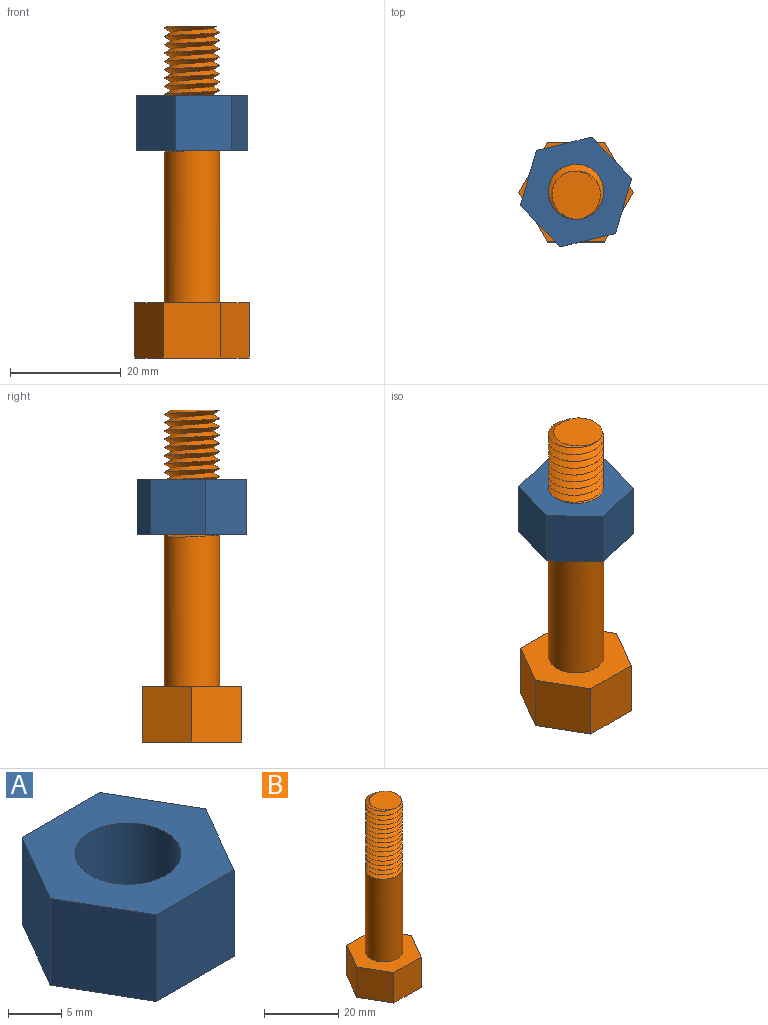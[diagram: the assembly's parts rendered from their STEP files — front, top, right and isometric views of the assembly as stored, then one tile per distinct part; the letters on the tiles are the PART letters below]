
ASSEMBLY  parts=2 mates=1
PART A: 9 faces, bbox 20.7x17.9x10 mm
  f0: plane 10x8.96mm, normal (0.87,-0.5,0), area 103.5mm2, adj f1,f5,f7,f8
  f1: plane 10x8.96mm, normal (0.87,0.5,0), area 103.5mm2, adj f0,f2,f7,f8
  f2: plane 10.35x10mm, normal (0,1,0), area 103.5mm2, adj f1,f3,f7,f8
  f3: plane 10x8.96mm, normal (-0.87,0.5,0), area 103.5mm2, adj f2,f4,f7,f8
  f4: plane 10x8.96mm, normal (-0.87,-0.5,0), area 103.5mm2, adj f3,f5,f7,f8
  f5: plane 10.35x10mm, normal (0,-1,0), area 103.5mm2, adj f0,f4,f7,f8
  f6: cylinder r=5mm len=10mm, axis (0,0,-1), area 314.2mm2, adj f7,f8
  f7: plane 20.7x17.93mm, normal (0,0,1), area 199.7mm2, adj f0,f1,f2,f3,f4,f5,f6
  f8: plane 20.7x17.93mm, normal (0,0,-1), area 199.7mm2, adj f0,f1,f2,f3,f4,f5,f6
PART B: 28 faces, bbox 21.8x19x61.9 mm
  f0: plane 10x8.96mm, normal (0.87,-0.5,0), area 103.5mm2, adj f1,f5,f6,f7
  f1: plane 10x8.96mm, normal (0.87,0.5,0), area 103.5mm2, adj f0,f2,f6,f7
  f2: plane 10.35x10mm, normal (0,1,0), area 103.5mm2, adj f1,f3,f6,f7
  f3: plane 10x8.96mm, normal (-0.87,0.5,0), area 103.5mm2, adj f2,f4,f6,f7
  f4: plane 10x8.96mm, normal (-0.87,-0.5,0), area 103.5mm2, adj f3,f5,f6,f7
  f5: plane 10.35x10mm, normal (0,-1,0), area 103.5mm2, adj f0,f4,f6,f7
  f6: plane 20.7x17.93mm, normal (0,0,1), area 199.7mm2, adj f0,f1,f2,f3,f4,f5,f8
  f7: plane 20.7x17.93mm, normal (0,0,-1), area 278.3mm2, adj f0,f1,f2,f3,f4,f5
  f8: cylinder r=5mm len=28.36mm, axis (0,0,-1), area 867.2mm2, adj f6,f23,f25,f27
  f9: cylinder r=5mm len=9.33mm, axis (0,0,-1), area 0.1mm2, adj f10,f24,f26,f27
  f10: cylinder r=5mm len=10mm, axis (0,0,-1), area 0.2mm2, adj f9,f11,f26,f27
  f11: cylinder r=5mm len=10mm, axis (0,0,-1), area 0.2mm2, adj f10,f12,f26,f27
  f12: cylinder r=5mm len=10mm, axis (0,0,-1), area 0.1mm2, adj f11,f13,f26,f27
  f13: cylinder r=5mm len=10mm, axis (0,0,-1), area 0.2mm2, adj f12,f14,f26,f27
  f14: cylinder r=5mm len=10mm, axis (0,0,-1), area 0.2mm2, adj f13,f15,f26,f27
  f15: cylinder r=5mm len=10mm, axis (0,0,-1), area 0.1mm2, adj f14,f16,f26,f27
  f16: cylinder r=5mm len=10mm, axis (0,0,-1), area 0.2mm2, adj f15,f17,f26,f27
  f17: cylinder r=5mm len=10mm, axis (0,0,-1), area 0.2mm2, adj f16,f18,f26,f27
  f18: cylinder r=5mm len=10mm, axis (0,0,-1), area 0.2mm2, adj f17,f19,f26,f27
  f19: cylinder r=5mm len=10mm, axis (0,0,-1), area 0.1mm2, adj f18,f20,f26,f27
  f20: cylinder r=5mm len=10mm, axis (0,0,-1), area 0.2mm2, adj f19,f21,f26,f27
  f21: cylinder r=5mm len=10mm, axis (0,0,-1), area 0.2mm2, adj f20,f22,f26,f27
  f22: cylinder r=5mm len=10mm, axis (0,0,-1), area 0.2mm2, adj f21,f23,f26,f27
  f23: cylinder r=5mm len=10mm, axis (0,0,-1), area 0.2mm2, adj f8,f22,f26,f27
  f24: plane 9.82x9.81mm, normal (0,0,1), area 60mm2, adj f9,f26,f27
  f25: plane 1.5x1.12mm, normal (-0.87,-0.5,0), area 1mm2, adj f8,f26,f27
  f26: bspline ~23.5x11.55mm, area 600.2mm2, adj f9,f10,f11,f12,f13,f14,f15,f16
  f27: bspline ~24.25x11.55mm, area 621.8mm2, adj f8,f9,f10,f11,f12,f13,f14,f15
PLACE A rot(axis=(0,0,1),133.6deg) t=(-4.81,-11.49,7.5)mm
PLACE B t=(-4.81,-11.49,-30)mm fixed
MATE cylindrical B.f8 <-> A.f6  axis (0,0,-1) through (-4.81,-11.49,5)mm
